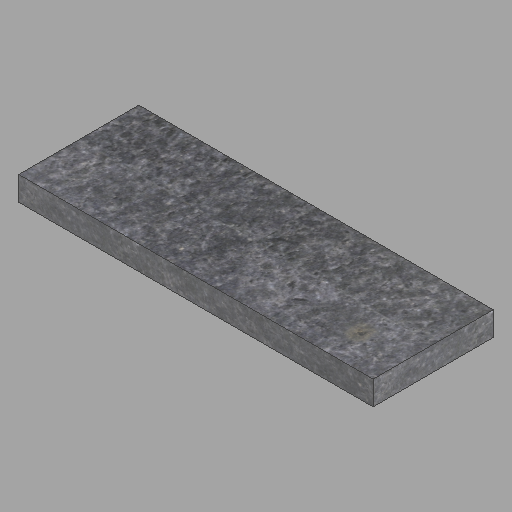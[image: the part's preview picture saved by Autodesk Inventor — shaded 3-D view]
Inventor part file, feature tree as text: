
AUTODESK INVENTOR PART (.ipt)
format: ipt  version: 2023 (Build 270158030, 158C)  size: 226,304 bytes
history: native  units: in
note: dims shown in document units (in); Inventor stores cm internally (conversion verified against a paired STEP export)
features: extrude x1, sketch x1
ambient origin geometry x8: Origin, YZ Plane, XZ Plane, XY Plane, X Axis, Y Axis, Z Axis, Center Point
bodies: Solid1 (feature_tree)
feature tree (2):
  extrude  "Extrusion1"  Depth=10.0in
  sketch  "Sketch1"  dims[d0=29.5in d1=10.0in d2=2.0in d3=0.0in]
